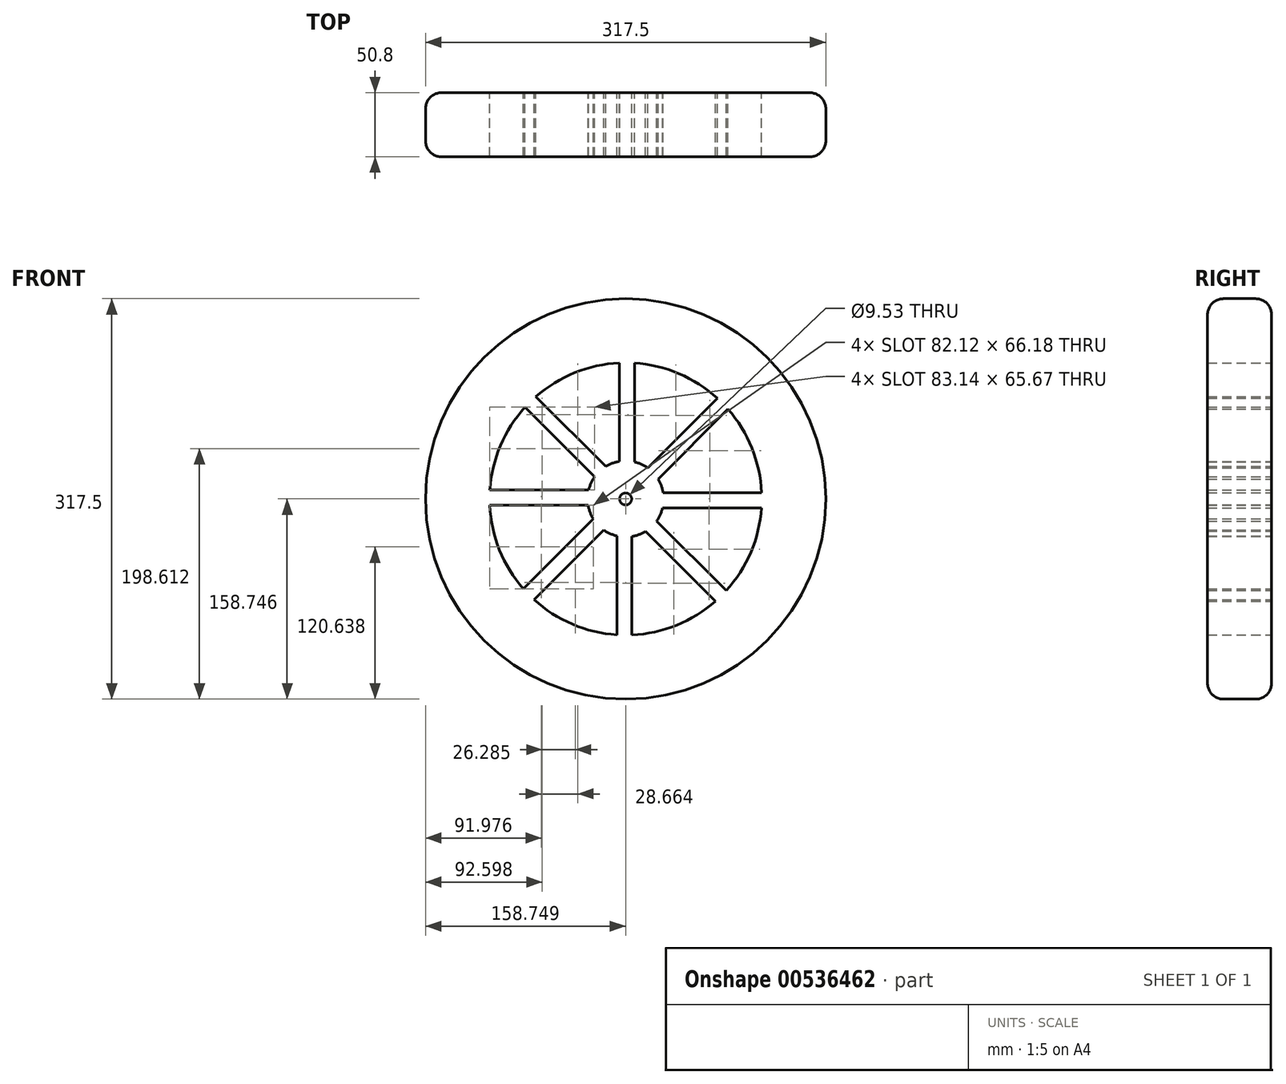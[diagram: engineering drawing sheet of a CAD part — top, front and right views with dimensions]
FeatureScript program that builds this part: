
annotation { "Feature Type Name" : "Feature", "Feature Type Description" : "" }
export const myFeature = defineFeature(function(context is Context, id is Id, definition is map)
    precondition{}
    {
        {
            var Q0;
            Q0=qCreatedBy(makeId("Front.planeOp"),FACE);
            var sketch = newSketch(context, id + "F0", { "sketchPlane" : qUnion([Q0])});
            skCircle(sketch, "E0", {"center": v(-53.95, 5.73) * mm, "radius": 158.75 * mm});
            skCircle(sketch, "E1", {"center": v(-53.95, 5.73) * mm, "radius": 4.76 * mm});
            skArc(sketch, "E2.0", {"start": v(-58.97, 113.56) * mm, "mid": v(-94.33, 105.84) * mm, "end": v(-125.15, 86.87) * mm});
            skArc(sketch, "E3.0", {"start": v(-36.47, 30.3) * mm, "mid": v(-41.47, 33.18) * mm, "end": v(-46.92, 35.06) * mm});
            skLineSegment(sketch, "E4.0", {"start": v(-46.92, 18.34) * mm, "end": v(-46.92, 19.86) * mm});
            skLineSegment(sketch, "E5.0", {"start": v(-58.97, 18.58) * mm, "end": v(-58.97, 20.69) * mm});
            skLineSegment(sketch, "E6.1.0", {"start": v(-57.9, 19.61) * mm, "end": v(-58.97, 20.69) * mm});
            skLineSegment(sketch, "E6.1.1", {"start": v(-66.59, 11.26) * mm, "end": v(-68.08, 12.76) * mm});
            skLineSegment(sketch, "E6.2.0", {"start": v(-66.56, 12.76) * mm, "end": v(-68.08, 12.76) * mm});
            skLineSegment(sketch, "E6.2.1", {"start": v(-66.8, 0.7) * mm, "end": v(-68.91, 0.7) * mm});
            skLineSegment(sketch, "E6.3.0", {"start": v(-67.84, 1.78) * mm, "end": v(-68.91, 0.7) * mm});
            skLineSegment(sketch, "E6.3.1", {"start": v(-59.49, -6.9) * mm, "end": v(-60.98, -8.4) * mm});
            skLineSegment(sketch, "E6.4.0", {"start": v(-60.98, -6.88) * mm, "end": v(-60.98, -8.4) * mm});
            skLineSegment(sketch, "E6.4.1", {"start": v(-48.93, -7.12) * mm, "end": v(-48.93, -9.24) * mm});
            skLineSegment(sketch, "E6.5.0", {"start": v(-50, -8.16) * mm, "end": v(-48.93, -9.24) * mm});
            skLineSegment(sketch, "E6.5.1", {"start": v(-41.32, 0.2) * mm, "end": v(-39.82, -1.3) * mm});
            skLineSegment(sketch, "E6.6.0", {"start": v(-41.34, -1.3) * mm, "end": v(-39.82, -1.3) * mm});
            skLineSegment(sketch, "E6.6.1", {"start": v(-41.1, 10.75) * mm, "end": v(-38.99, 10.75) * mm});
            skLineSegment(sketch, "E6.7.0", {"start": v(-40.06, 9.67) * mm, "end": v(-38.99, 10.75) * mm});
            skLineSegment(sketch, "E6.7.1", {"start": v(-48.41, 18.36) * mm, "end": v(-46.92, 19.86) * mm});
            skLineSegment(sketch, "E7.trimOffspring", {"start": v(-36.47, 30.3) * mm, "end": v(14.45, 81.22) * mm});
            skLineSegment(sketch, "E8.trimOffspring", {"start": v(-28.24, 21.5) * mm, "end": v(22.8, 72.53) * mm});
            skLineSegment(sketch, "E9.trimOffspring", {"start": v(-46.92, 35.06) * mm, "end": v(-46.92, 107.24) * mm});
            skLineSegment(sketch, "E10.trimOffspring", {"start": v(-58.97, 35.47) * mm, "end": v(-58.97, 107.48) * mm});
            skLineSegment(sketch, "E11.trimOffspring", {"start": v(-69.72, 31.44) * mm, "end": v(-120.76, 82.48) * mm});
            skLineSegment(sketch, "E12.trimOffspring", {"start": v(-83.28, 12.76) * mm, "end": v(-155.46, 12.76) * mm});
            skLineSegment(sketch, "E13.trimOffspring", {"start": v(-78.53, 23.2) * mm, "end": v(-129.45, 74.12) * mm});
            skArc(sketch, "E14.trimOffspring", {"start": v(-78.53, 23.2) * mm, "mid": v(-81.4, 18.21) * mm, "end": v(-83.28, 12.76) * mm});
            skArc(sketch, "E15.trimOffspring", {"start": v(-58.97, 35.47) * mm, "mid": v(-64.54, 33.97) * mm, "end": v(-69.72, 31.44) * mm});
            skArc(sketch, "E16.trimOffspring", {"start": v(-83.7, 0.7) * mm, "mid": v(-82.2, -4.86) * mm, "end": v(-79.66, -10.04) * mm});
            skLineSegment(sketch, "E17.trimOffspring", {"start": v(-83.7, 0.7) * mm, "end": v(-155.7, 0.7) * mm});
            skLineSegment(sketch, "E18.trimOffspring", {"start": v(-79.66, -10.04) * mm, "end": v(-130.7, -61.08) * mm});
            skLineSegment(sketch, "E19.trimOffspring", {"start": v(-71.43, -18.85) * mm, "end": v(-122.35, -69.77) * mm});
            skArc(sketch, "E20.trimOffspring", {"start": v(-71.43, -18.85) * mm, "mid": v(-66.44, -21.73) * mm, "end": v(-60.98, -23.6) * mm});
            skLineSegment(sketch, "E21.trimOffspring", {"start": v(-60.98, -23.6) * mm, "end": v(-60.98, -95.78) * mm});
            skArc(sketch, "E22.trimOffspring", {"start": v(-48.93, -24.02) * mm, "mid": v(-43.36, -22.52) * mm, "end": v(-38.18, -19.99) * mm});
            skLineSegment(sketch, "E23.trimOffspring", {"start": v(-48.93, -24.02) * mm, "end": v(-48.93, -96.02) * mm});
            skLineSegment(sketch, "E24.trimOffspring", {"start": v(-38.18, -19.99) * mm, "end": v(12.86, -71.02) * mm});
            skLineSegment(sketch, "E25.trimOffspring", {"start": v(-29.37, -11.76) * mm, "end": v(21.54, -62.67) * mm});
            skLineSegment(sketch, "E26.trimOffspring", {"start": v(-24.62, -1.3) * mm, "end": v(47.56, -1.3) * mm});
            skLineSegment(sketch, "E27.trimOffspring", {"start": v(-24.2, 10.75) * mm, "end": v(47.8, 10.75) * mm});
            skArc(sketch, "E28.trimOffspring", {"start": v(-24.2, 10.75) * mm, "mid": v(-25.7, 16.31) * mm, "end": v(-28.24, 21.5) * mm});
            skArc(sketch, "E29.trimOffspring", {"start": v(-29.37, -11.76) * mm, "mid": v(-26.5, -6.76) * mm, "end": v(-24.62, -1.3) * mm});
            skArc(sketch, "E30.trimOffspring", {"start": v(-133.75, 78.43) * mm, "mid": v(-153.3, 47.97) * mm, "end": v(-161.67, 12.76) * mm});
            skArc(sketch, "E31.trimOffspring", {"start": v(-161.78, 0.7) * mm, "mid": v(-154.07, -34.65) * mm, "end": v(-135.1, -65.47) * mm});
            skArc(sketch, "E32.trimOffspring", {"start": v(18.75, 85.53) * mm, "mid": v(-11.71, 105.07) * mm, "end": v(-46.92, 113.45) * mm});
            skArc(sketch, "E33.trimOffspring", {"start": v(53.88, 10.75) * mm, "mid": v(46.16, 46.1) * mm, "end": v(27.2, 76.93) * mm});
            skArc(sketch, "E34.trimOffspring", {"start": v(25.85, -66.97) * mm, "mid": v(45.4, -36.51) * mm, "end": v(53.77, -1.3) * mm});
            skArc(sketch, "E35.trimOffspring", {"start": v(-48.93, -102.1) * mm, "mid": v(-13.57, -94.39) * mm, "end": v(17.25, -75.42) * mm});
            skArc(sketch, "E36.trimOffspring", {"start": v(-126.65, -74.07) * mm, "mid": v(-96.2, -93.62) * mm, "end": v(-60.98, -102) * mm});
            skLineSegment(sketch, "E37", {"start": v(-155.46, 12.76) * mm, "end": v(-161.67, 12.76) * mm});
            skLineSegment(sketch, "E38", {"start": v(-155.7, 0.7) * mm, "end": v(-161.78, 0.7) * mm});
            skLineSegment(sketch, "E39", {"start": v(-130.7, -61.08) * mm, "end": v(-135.1, -65.47) * mm});
            skLineSegment(sketch, "E40", {"start": v(-122.35, -69.77) * mm, "end": v(-126.65, -74.07) * mm});
            skLineSegment(sketch, "E41", {"start": v(-129.45, 74.12) * mm, "end": v(-133.75, 78.43) * mm});
            skLineSegment(sketch, "E42", {"start": v(-120.76, 82.48) * mm, "end": v(-125.15, 86.87) * mm});
            skLineSegment(sketch, "E43", {"start": v(-58.97, 107.48) * mm, "end": v(-58.97, 113.56) * mm});
            skLineSegment(sketch, "E44", {"start": v(-46.92, 107.24) * mm, "end": v(-46.92, 113.45) * mm});
            skLineSegment(sketch, "E45", {"start": v(14.45, 81.22) * mm, "end": v(18.75, 85.53) * mm});
            skLineSegment(sketch, "E46", {"start": v(27.2, 76.93) * mm, "end": v(22.8, 72.53) * mm});
            skLineSegment(sketch, "E47", {"start": v(47.8, 10.75) * mm, "end": v(53.88, 10.75) * mm});
            skLineSegment(sketch, "E48", {"start": v(47.56, -1.3) * mm, "end": v(53.77, -1.3) * mm});
            skLineSegment(sketch, "E49", {"start": v(12.86, -71.02) * mm, "end": v(17.25, -75.42) * mm});
            skLineSegment(sketch, "E50", {"start": v(-48.93, -96.02) * mm, "end": v(-48.93, -102.1) * mm});
            skLineSegment(sketch, "E51", {"start": v(21.54, -62.67) * mm, "end": v(25.85, -66.97) * mm});
            skLineSegment(sketch, "E52", {"start": v(-60.98, -95.78) * mm, "end": v(-60.98, -102) * mm});
            skSolve(sketch);
        }
        {
            var Q0;
            Q0 = qSketchRegion(id + "F0", true);
            extrude(context, id + "F1", {"entities" : qUnion([Q0]), "depth" : 50.8 * mm, "offsetDistance" : 25.4 * mm});
        }
        {
            var Q0;
            Q0=makeQuery(id+"F1.opExtrude","CAP_EDGE",EDGE,{"disambiguationData":[OSD([sQuery(id+"F0.wireOp",EDGE,"E0")])],"isStart":false});
            var Q1;
            Q1=makeQuery(id+"F1.opExtrude","CAP_EDGE",EDGE,{"disambiguationData":[OSD([sQuery(id+"F0.wireOp",EDGE,"E0")])],"isStart":true});
            fillet(context, id + "F2", {"entities" : qUnion([Q0, Q1]), "radius" : 12.7 * mm, "tangentPropagation" : true, "allowEdgeOverflow" : false});
        }
    });
